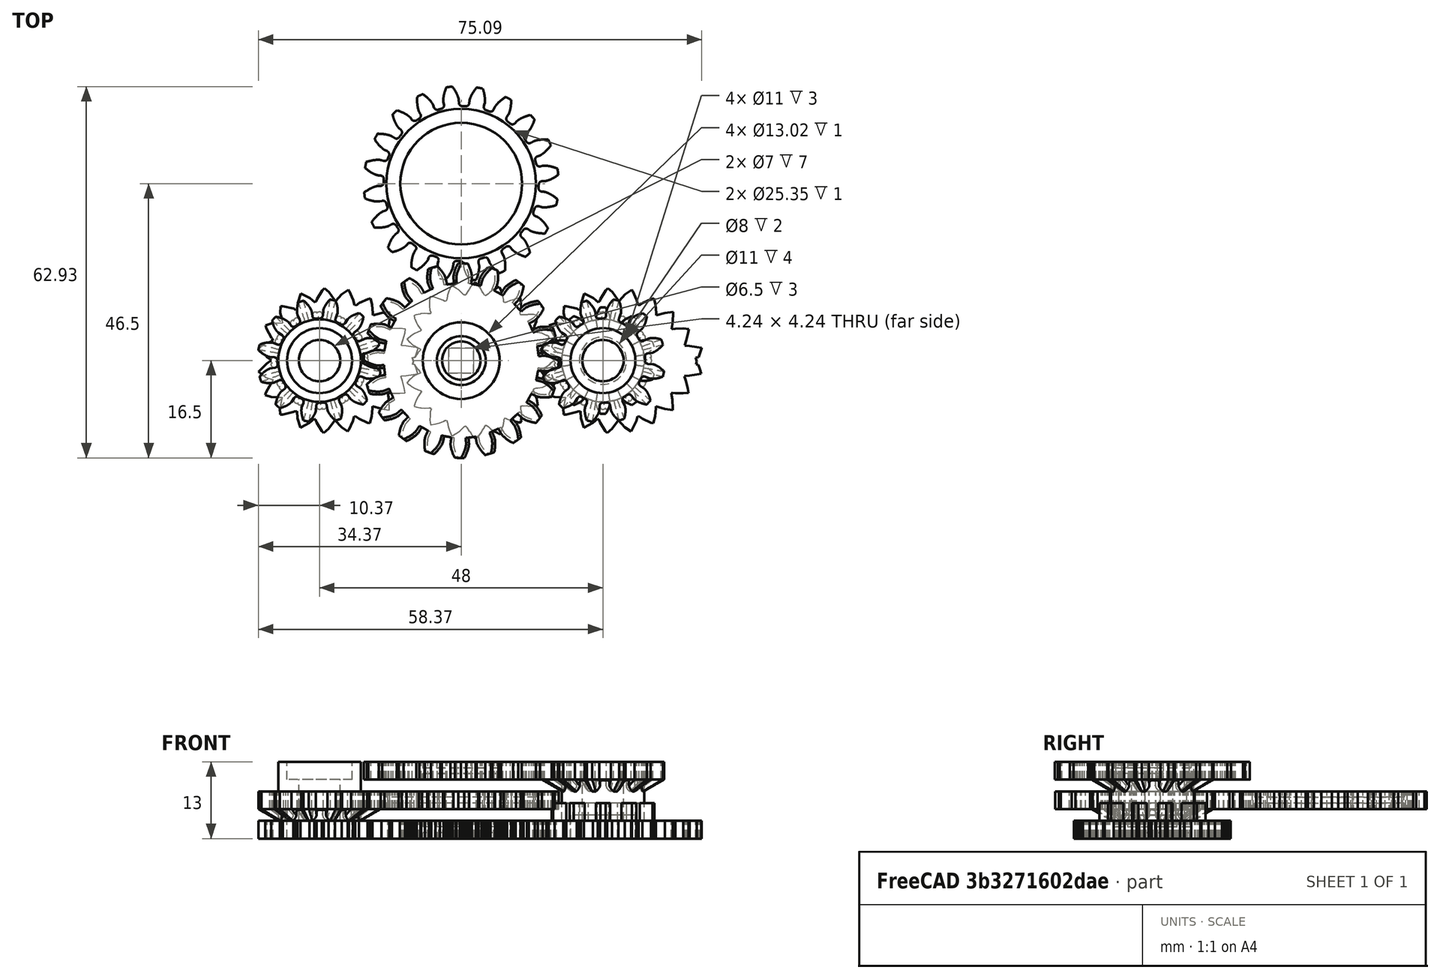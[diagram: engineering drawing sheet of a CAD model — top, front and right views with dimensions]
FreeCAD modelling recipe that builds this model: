
FCSTD DOCUMENT  (FreeCAD 0.16RUnknown)
Label: TriangleWaveGears
License: All rights reserved
LicenseURL: http://en.wikipedia.org/wiki/All_rights_reserved
objects: Sketcher::SketchObject×13, Part::Part2DObjectPython×11, Part::Cut×10, Part::Cylinder×9, PartDesign::Pad×8, Part::MultiFuse×7, PartDesign::Revolution×6, Part::FeaturePython×3, Mesh::Feature×2, Part::Loft×2
note: 83 computed .brp shape members not serialized (recipe doc carries the construction recipe); baked Part::Feature solids carry a one-line shape summary decoded from their .brp

FEATURE [Part::Part2DObjectPython] DWire  # Draft 2D object (typed FeaturePython)
  ChamferSize = 0
  Closed = true
  End = (40.7092,2.14552,0)
  FilletRadius = 0
  Length = 116.74
  MakeFace = true
  Placement = pos=(24,0,0) rot=(0,0,1;0rad)
  Points = (141) [(16.719,2.12868,0),(16.7092,2.14552,0),(15.8889,2.29087,0),(14.6751,2.46439,0),(13.876,2.52602,0),(13.8894,2.57671,0),(13.8323,2.58486,0),+134 more]
  Start = (40.719,2.12868,0)
  Subdivisions = 0
FEATURE [PartDesign::Pad] Pad
  Length = 3
  Length2 = 100
  Placement = pos=(24,0,0) rot=(0,0,1;0rad)
  Sketch = -> DWire
  Type = 0
FEATURE [Part::Part2DObjectPython] DWire001  # Draft 2D object (typed FeaturePython)
  ChamferSize = 0
  Closed = true
  End = (12.9776,-7.52391,0)
  FilletRadius = 0
  Length = 115.99
  MakeFace = true
  Points = (347) [(12.9407,-7.5751,0),(12.9776,-7.52391,0),(12.7586,-6.44106,0),(12.4722,-5.82977,0),(12.4305,-5.55586,0),(12.1811,-4.95491,0),(12.3268,-4.87553,0),+340 more]
  Start = (12.9407,-7.5751,0)
  Subdivisions = 0
FEATURE [PartDesign::Pad] Pad001
  Length = 3
  Length2 = 100
  Sketch = -> DWire001
  Type = 0
FEATURE [Sketcher::SketchObject] Sketch
  sketch-geometry (6):
    g0: LineSegment StartX=2.12132 StartY=2.12132 StartZ=0 EndX=-2.12132 EndY=2.12132 EndZ=0
    g1: LineSegment StartX=-2.12132 StartY=2.12132 StartZ=0 EndX=-2.12132 EndY=-2.12132 EndZ=0
    g2: LineSegment StartX=-2.12132 StartY=-2.12132 StartZ=0 EndX=2.12132 EndY=-2.12132 EndZ=0
    g3: LineSegment StartX=2.12132 StartY=-2.12132 StartZ=0 EndX=2.12132 EndY=2.12132 EndZ=0
    g4: Circle [constr] CenterX=0 CenterY=0 CenterZ=0 NormalX=0 NormalY=0 NormalZ=1 Radius=3
    g5: LineSegment [constr] StartX=0 StartY=0 StartZ=0 EndX=2.12132 EndY=2.12132 EndZ=0
  constraints (16):
    c: Coincident(g0,g1)
    c: Coincident(g1,g2)
    c: Coincident(g2,g3)
    c: Coincident(g3,g0)
    c: Equal(g0,g1)
    c: Equal(g0,g2)
    c: Equal(g0,g3)
    c: PointOnObject(g0,g4)
    c: PointOnObject(g1,g4)
    c: PointOnObject(g2,g4)
    c: PointOnObject(g3,g4)
    c: Coincident(g4,g-1)
    c: Radius(g4) = 3
    c: Coincident(g5,g-1)
    c: Coincident(g5,g0)
    c: Angle(g-1,g5) = 0.785398
FEATURE [PartDesign::Pad] Pad002
  Length = 10
  Length2 = 100
  Sketch = -> Sketch
  Type = 0
FEATURE [Part::Cut] Cut
  Base = -> Pad001
  Tool = -> Pad002
FEATURE [Sketcher::SketchObject] Sketch001
  Placement = pos=(24,0,0) rot=(0,0,1;0rad)
  sketch-geometry (1):
    g0: Circle CenterX=0 CenterY=0 CenterZ=0 NormalX=0 NormalY=0 NormalZ=1 Radius=5.5
  constraints (2):
    c: Coincident(g0,g-1)
    c: Radius(g0) = 5.5
FEATURE [PartDesign::Pad] Pad003
  Length = 4
  Length2 = 100
  Placement = pos=(24,0,0) rot=(0,0,1;0rad)
  Sketch = -> Sketch001
  Type = 0
FEATURE [Sketcher::SketchObject] Sketch002
  Placement = pos=(24,0,0) rot=(0,0,1;0rad)
  sketch-geometry (1):
    g0: Circle CenterX=0 CenterY=0 CenterZ=0 NormalX=0 NormalY=0 NormalZ=1 Radius=4
  constraints (2):
    c: Coincident(g0,g-1)
    c: Radius(g0) = 4
FEATURE [PartDesign::Pad] Pad004
  Length = 10
  Length2 = 100
  Placement = pos=(24,0,0) rot=(0,0,1;0rad)
  Sketch = -> Sketch002
  Type = 0
FEATURE [Part::FeaturePython] InvoluteGear  # WARN: FeaturePython — macro-defined, semantics opaque (R4)
  Placement = pos=(24,0,3) rot=(0,0,1;0.314159rad)
  backlash = 0
  beta = 0
  clearance = 0.25
  height = 3
  module = 1.5
  numpoints = 6
  pressure_angle = 20
  shift = 0
  simple = false
  teeth = 10
  undercut = false
FEATURE [Part::FeaturePython] InvoluteGear001  # WARN: FeaturePython — macro-defined, semantics opaque (R4)
  Placement = pos=(0,0,9) rot=(0,0,1;0.087266rad)
  backlash = 0
  beta = 0
  clearance = 0.25
  height = 3
  module = 1.5
  numpoints = 6
  pressure_angle = 20
  shift = 0
  simple = false
  teeth = 20
  undercut = false
FEATURE [Mesh::Feature] PD_inner_gear
  Placement = pos=(0,-33,7) rot=(0,0,1;0rad)
FEATURE [Part::FeaturePython] InvoluteGear002  # WARN: FeaturePython — macro-defined, semantics opaque (R4)
  Placement = pos=(0,0,5) rot=(0,0,1;0rad)
  backlash = 0
  beta = 0
  clearance = 0.25
  height = 3
  module = 1.5
  numpoints = 6
  pressure_angle = 20
  shift = 0
  simple = false
  teeth = 20
  undercut = false
FEATURE [Mesh::Feature] PD_inner_gear001
  Placement = pos=(0,-33,11) rot=(0,0,1;0rad)
FEATURE [Part::MultiFuse] Fusion
  Shapes = -> [Pad004,Pad003]
FEATURE [Part::MultiFuse] Fusion001
  Shapes = -> [InvoluteGear,Pad]
FEATURE [Part::Cut] Cut001
  Base = -> Fusion001
  Tool = -> Fusion
FEATURE [Sketcher::SketchObject] Sketch003
  Placement = pos=(0,0,8) rot=(1,0,0;1.5708rad)
  sketch-geometry (16):
    g0: Circle [constr] CenterX=0 CenterY=0 CenterZ=0 NormalX=0 NormalY=0 NormalZ=1 Radius=5.3242
    g1: Circle [constr] CenterX=5.3242 CenterY=0 CenterZ=0 NormalX=0 NormalY=0 NormalZ=1 Radius=1.5
    g2: Circle [constr] CenterX=4.479 CenterY=-2.87848 CenterZ=0 NormalX=0 NormalY=0 NormalZ=1 Radius=1.5
    g3: LineSegment [constr] StartX=0 StartY=0 StartZ=0 EndX=4.479 EndY=-2.87848 EndZ=0
    g4: LineSegment StartX=4.13993 StartY=1 StartZ=0 EndX=6.50847 EndY=1 EndZ=0
    g5: LineSegment StartX=6.50847 StartY=1 StartZ=0 EndX=6.50847 EndY=2 EndZ=0
    g6: LineSegment StartX=6.50847 StartY=2 StartZ=0 EndX=4.13993 EndY=2 EndZ=0
    g7: LineSegment StartX=4.13993 StartY=2 StartZ=0 EndX=4.13993 EndY=1 EndZ=0
    g8: LineSegment [constr] StartX=4.13993 StartY=-1 StartZ=0 EndX=6.50847 EndY=-1 EndZ=0
    g9: LineSegment [constr] StartX=6.50847 StartY=-1 StartZ=0 EndX=6.50847 EndY=-2 EndZ=0
    g10: LineSegment [constr] StartX=6.50847 StartY=-2 StartZ=0 EndX=4.13993 EndY=-2 EndZ=0
    g11: LineSegment [constr] StartX=4.13993 StartY=-2 StartZ=0 EndX=4.13993 EndY=-1 EndZ=0
    g12: LineSegment [constr] StartX=5.3242 StartY=0 StartZ=0 EndX=5.3242 EndY=2 EndZ=0
    g13: Circle [constr] CenterX=5.3242 CenterY=0 CenterZ=0 NormalX=0 NormalY=0 NormalZ=1 Radius=1.55
    g14: LineSegment [constr] StartX=5.3242 StartY=0 StartZ=0 EndX=6.769 EndY=-0.403161 EndZ=0
    g15: LineSegment [constr] StartX=6.769 StartY=-0.403161 StartZ=0 EndX=6.81716 EndY=-0.416599 EndZ=0
  constraints (42):
    c: Coincident(g0,g-1)
    c: PointOnObject(g1,g0)
    c: PointOnObject(g2,g0)
    c: Tangent(g1,g2)
    c: Equal(g1,g2)
    c: Coincident(g3,g-1)
    c: Coincident(g3,g2)
    c: Angle(g3,g-1) = 0.571199
    c: Radius(g1) = 1.5
    c: PointOnObject(g1,g-1)
    c: Horizontal(g4)
    c: Coincident(g4,g5)
    c: Vertical(g5)
    c: Coincident(g5,g6)
    c: Coincident(g6,g7)
    c: Coincident(g7,g4)
    c: Vertical(g7)
    c: Horizontal(g6)
    c: Coincident(g8,g9)
    c: Coincident(g9,g10)
    c: Coincident(g10,g11)
    c: Coincident(g11,g8)
    c: Horizontal(g8)
    c: Horizontal(g10)
    c: Vertical(g9)
    c: Vertical(g11)
    c: Symmetric(g8,g4,g-1)
    c: DistanceY(g8,g4) = 2
    c: Coincident(g12,g1)
    c: PointOnObject(g12,g6)
    c: Symmetric(g6,g5,g12)
    c: Equal(g4,g8)
    c: Equal(g5,g9)
    c: DistanceY(g5,g5) = 1
    c: Coincident(g13,g1)
    c: Coincident(g14,g1)
    c: Coincident(g14,g15)
    c: PointOnObject(g15,g13)
    c: PointOnObject(g14,g1)
    c: Parallel(g15,g14)
    c: Distance(g15) = 0.05
    c: PointOnObject(g4,g13)
FEATURE [PartDesign::Revolution] Revolution
  Angle = 360
  Axis = (0,0,1)
  Base = (0,0,8)
  Placement = pos=(0,0,8) rot=(1,0,0;1.5708rad)
  ReferenceAxis = -> Sketch003 [V_Axis]
  Reversed = true
  Sketch = -> Sketch003
FEATURE [Part::Cut] Cut002
  Base = -> InvoluteGear001
  Tool = -> Revolution
FEATURE [Sketcher::SketchObject] Sketch004
  Placement = pos=(0,0,13) rot=(1,0,0;1.5708rad)
  sketch-geometry (16):
    g0: Circle [constr] CenterX=0 CenterY=0 CenterZ=0 NormalX=0 NormalY=0 NormalZ=1 Radius=5.3242
    g1: Circle [constr] CenterX=5.3242 CenterY=0 CenterZ=0 NormalX=0 NormalY=0 NormalZ=1 Radius=1.5
    g2: Circle [constr] CenterX=4.479 CenterY=-2.87848 CenterZ=0 NormalX=0 NormalY=0 NormalZ=1 Radius=1.5
    g3: LineSegment [constr] StartX=0 StartY=0 StartZ=0 EndX=4.479 EndY=-2.87848 EndZ=0
    g4: LineSegment [constr] StartX=4.13993 StartY=1 StartZ=0 EndX=6.50847 EndY=1 EndZ=0
    g5: LineSegment [constr] StartX=6.50847 StartY=1 StartZ=0 EndX=6.50847 EndY=2 EndZ=0
    g6: LineSegment [constr] StartX=6.50847 StartY=2 StartZ=0 EndX=4.13993 EndY=2 EndZ=0
    g7: LineSegment [constr] StartX=4.13993 StartY=2 StartZ=0 EndX=4.13993 EndY=1 EndZ=0
    g8: LineSegment StartX=4.13993 StartY=-1 StartZ=0 EndX=6.50847 EndY=-1 EndZ=0
    g9: LineSegment StartX=6.50847 StartY=-1 StartZ=0 EndX=6.50847 EndY=-2 EndZ=0
    g10: LineSegment StartX=6.50847 StartY=-2 StartZ=0 EndX=4.13993 EndY=-2 EndZ=0
    g11: LineSegment StartX=4.13993 StartY=-2 StartZ=0 EndX=4.13993 EndY=-1 EndZ=0
    g12: LineSegment [constr] StartX=5.3242 StartY=0 StartZ=0 EndX=5.3242 EndY=2 EndZ=0
    g13: Circle [constr] CenterX=5.3242 CenterY=0 CenterZ=0 NormalX=0 NormalY=0 NormalZ=1 Radius=1.55
    g14: LineSegment [constr] StartX=5.3242 StartY=0 StartZ=0 EndX=6.769 EndY=-0.403179 EndZ=0
    g15: LineSegment [constr] StartX=6.769 StartY=-0.403179 StartZ=0 EndX=6.81716 EndY=-0.416618 EndZ=0
  constraints (42):
    c: Coincident(g0,g-1)
    c: PointOnObject(g1,g0)
    c: PointOnObject(g2,g0)
    c: Tangent(g1,g2)
    c: Equal(g1,g2)
    c: Coincident(g3,g-1)
    c: Coincident(g3,g2)
    c: Angle(g3,g-1) = 0.571199
    c: Radius(g1) = 1.5
    c: PointOnObject(g1,g-1)
    c: Horizontal(g4)
    c: Coincident(g4,g5)
    c: Vertical(g5)
    c: Coincident(g5,g6)
    c: Coincident(g6,g7)
    c: Coincident(g7,g4)
    c: Vertical(g7)
    c: Horizontal(g6)
    c: Coincident(g8,g9)
    c: Coincident(g9,g10)
    c: Coincident(g10,g11)
    c: Coincident(g11,g8)
    c: Horizontal(g8)
    c: Horizontal(g10)
    c: Vertical(g9)
    c: Vertical(g11)
    c: Symmetric(g8,g4,g-1)
    c: DistanceY(g8,g4) = 2
    c: Coincident(g12,g1)
    c: PointOnObject(g12,g6)
    c: Symmetric(g6,g5,g12)
    c: Equal(g4,g8)
    c: Equal(g5,g9)
    c: DistanceY(g5,g5) = 1
    c: Coincident(g13,g1)
    c: Coincident(g14,g1)
    c: Coincident(g14,g15)
    c: PointOnObject(g15,g13)
    c: PointOnObject(g14,g1)
    c: Parallel(g15,g14)
    c: Distance(g15) = 0.05
    c: PointOnObject(g4,g13)
FEATURE [PartDesign::Revolution] Revolution001
  Angle = 360
  Axis = (0,0,1)
  Base = (0,0,13)
  Placement = pos=(0,0,13) rot=(1,0,0;1.5708rad)
  ReferenceAxis = -> Sketch004 [V_Axis]
  Reversed = true
  Sketch = -> Sketch004
FEATURE [Part::Cut] Cut003
  Base = -> Cut002
  Placement = pos=(0,0,1) rot=(0,0,1;0.191986rad)
  Tool = -> Revolution001
FEATURE [Sketcher::SketchObject] Sketch005
  sketch-geometry (1):
    g0: Circle CenterX=0 CenterY=0 CenterZ=0 NormalX=0 NormalY=0 NormalZ=1 Radius=4.5
  constraints (2):
    c: Coincident(g0,g-1)
    c: Radius(g0) = 4.5
FEATURE [Sketcher::SketchObject] Sketch007
  Placement = pos=(0,0,4) rot=(1,0,0;1.5708rad)
  sketch-geometry (16):
    g0: Circle [constr] CenterX=0 CenterY=0 CenterZ=0 NormalX=0 NormalY=0 NormalZ=1 Radius=5.3242
    g1: Circle [constr] CenterX=5.3242 CenterY=0 CenterZ=0 NormalX=0 NormalY=0 NormalZ=1 Radius=1.5
    g2: Circle [constr] CenterX=4.479 CenterY=-2.87848 CenterZ=0 NormalX=0 NormalY=0 NormalZ=1 Radius=1.5
    g3: LineSegment [constr] StartX=0 StartY=0 StartZ=0 EndX=4.479 EndY=-2.87848 EndZ=0
    g4: LineSegment [constr] StartX=4.13993 StartY=1 StartZ=0 EndX=6.50847 EndY=1 EndZ=0
    g5: LineSegment [constr] StartX=6.50847 StartY=1 StartZ=0 EndX=6.50847 EndY=2 EndZ=0
    g6: LineSegment [constr] StartX=6.50847 StartY=2 StartZ=0 EndX=4.13993 EndY=2 EndZ=0
    g7: LineSegment [constr] StartX=4.13993 StartY=2 StartZ=0 EndX=4.13993 EndY=1 EndZ=0
    g8: LineSegment StartX=4.13993 StartY=-1 StartZ=0 EndX=6.50847 EndY=-1 EndZ=0
    g9: LineSegment StartX=6.50847 StartY=-1 StartZ=0 EndX=6.50847 EndY=-2 EndZ=0
    g10: LineSegment StartX=6.50847 StartY=-2 StartZ=0 EndX=4.13993 EndY=-2 EndZ=0
    g11: LineSegment StartX=4.13993 StartY=-2 StartZ=0 EndX=4.13993 EndY=-1 EndZ=0
    g12: LineSegment [constr] StartX=5.3242 StartY=0 StartZ=0 EndX=5.3242 EndY=2 EndZ=0
    g13: Circle [constr] CenterX=5.3242 CenterY=0 CenterZ=0 NormalX=0 NormalY=0 NormalZ=1 Radius=1.55
    g14: LineSegment [constr] StartX=5.3242 StartY=0 StartZ=0 EndX=6.769 EndY=-0.403179 EndZ=0
    g15: LineSegment [constr] StartX=6.769 StartY=-0.403179 StartZ=0 EndX=6.81716 EndY=-0.416618 EndZ=0
  constraints (42):
    c: Coincident(g0,g-1)
    c: PointOnObject(g1,g0)
    c: PointOnObject(g2,g0)
    c: Tangent(g1,g2)
    c: Equal(g1,g2)
    c: Coincident(g3,g-1)
    c: Coincident(g3,g2)
    c: Angle(g3,g-1) = 0.571199
    c: Radius(g1) = 1.5
    c: PointOnObject(g1,g-1)
    c: Horizontal(g4)
    c: Coincident(g4,g5)
    c: Vertical(g5)
    c: Coincident(g5,g6)
    c: Coincident(g6,g7)
    c: Coincident(g7,g4)
    c: Vertical(g7)
    c: Horizontal(g6)
    c: Coincident(g8,g9)
    c: Coincident(g9,g10)
    c: Coincident(g10,g11)
    c: Coincident(g11,g8)
    c: Horizontal(g8)
    c: Horizontal(g10)
    c: Vertical(g9)
    c: Vertical(g11)
    c: Symmetric(g8,g4,g-1)
    c: DistanceY(g8,g4) = 2
    c: Coincident(g12,g1)
    c: PointOnObject(g12,g6)
    c: Symmetric(g6,g5,g12)
    c: Equal(g4,g8)
    c: Equal(g5,g9)
    c: DistanceY(g5,g5) = 1
    c: Coincident(g13,g1)
    c: Coincident(g14,g1)
    c: Coincident(g14,g15)
    c: PointOnObject(g15,g13)
    c: PointOnObject(g14,g1)
    c: Parallel(g15,g14)
    c: Distance(g15) = 0.05
    c: PointOnObject(g4,g13)
FEATURE [Sketcher::SketchObject] Sketch008
  Placement = pos=(0,0,-1) rot=(1,0,0;1.5708rad)
  sketch-geometry (16):
    g0: Circle [constr] CenterX=0 CenterY=0 CenterZ=0 NormalX=0 NormalY=0 NormalZ=1 Radius=5.3242
    g1: Circle [constr] CenterX=5.3242 CenterY=0 CenterZ=0 NormalX=0 NormalY=0 NormalZ=1 Radius=1.5
    g2: Circle [constr] CenterX=4.479 CenterY=-2.87848 CenterZ=0 NormalX=0 NormalY=0 NormalZ=1 Radius=1.5
    g3: LineSegment [constr] StartX=0 StartY=0 StartZ=0 EndX=4.479 EndY=-2.87848 EndZ=0
    g4: LineSegment StartX=4.13993 StartY=1 StartZ=0 EndX=6.50847 EndY=1 EndZ=0
    g5: LineSegment StartX=6.50847 StartY=1 StartZ=0 EndX=6.50847 EndY=2 EndZ=0
    g6: LineSegment StartX=6.50847 StartY=2 StartZ=0 EndX=4.13993 EndY=2 EndZ=0
    g7: LineSegment StartX=4.13993 StartY=2 StartZ=0 EndX=4.13993 EndY=1 EndZ=0
    g8: LineSegment [constr] StartX=4.13993 StartY=-1 StartZ=0 EndX=6.50847 EndY=-1 EndZ=0
    g9: LineSegment [constr] StartX=6.50847 StartY=-1 StartZ=0 EndX=6.50847 EndY=-2 EndZ=0
    g10: LineSegment [constr] StartX=6.50847 StartY=-2 StartZ=0 EndX=4.13993 EndY=-2 EndZ=0
    g11: LineSegment [constr] StartX=4.13993 StartY=-2 StartZ=0 EndX=4.13993 EndY=-1 EndZ=0
    g12: LineSegment [constr] StartX=5.3242 StartY=0 StartZ=0 EndX=5.3242 EndY=2 EndZ=0
    g13: Circle [constr] CenterX=5.3242 CenterY=0 CenterZ=0 NormalX=0 NormalY=0 NormalZ=1 Radius=1.55
    g14: LineSegment [constr] StartX=5.3242 StartY=0 StartZ=0 EndX=6.769 EndY=-0.403161 EndZ=0
    g15: LineSegment [constr] StartX=6.769 StartY=-0.403161 StartZ=0 EndX=6.81716 EndY=-0.416599 EndZ=0
  constraints (42):
    c: Coincident(g0,g-1)
    c: PointOnObject(g1,g0)
    c: PointOnObject(g2,g0)
    c: Tangent(g1,g2)
    c: Equal(g1,g2)
    c: Coincident(g3,g-1)
    c: Coincident(g3,g2)
    c: Angle(g3,g-1) = 0.571199
    c: Radius(g1) = 1.5
    c: PointOnObject(g1,g-1)
    c: Horizontal(g4)
    c: Coincident(g4,g5)
    c: Vertical(g5)
    c: Coincident(g5,g6)
    c: Coincident(g6,g7)
    c: Coincident(g7,g4)
    c: Vertical(g7)
    c: Horizontal(g6)
    c: Coincident(g8,g9)
    c: Coincident(g9,g10)
    c: Coincident(g10,g11)
    c: Coincident(g11,g8)
    c: Horizontal(g8)
    c: Horizontal(g10)
    c: Vertical(g9)
    c: Vertical(g11)
    c: Symmetric(g8,g4,g-1)
    c: DistanceY(g8,g4) = 2
    c: Coincident(g12,g1)
    c: PointOnObject(g12,g6)
    c: Symmetric(g6,g5,g12)
    c: Equal(g4,g8)
    c: Equal(g5,g9)
    c: DistanceY(g5,g5) = 1
    c: Coincident(g13,g1)
    c: Coincident(g14,g1)
    c: Coincident(g14,g15)
    c: PointOnObject(g15,g13)
    c: PointOnObject(g14,g1)
    c: Parallel(g15,g14)
    c: Distance(g15) = 0.05
    c: PointOnObject(g4,g13)
FEATURE [PartDesign::Revolution] Revolution002
  Angle = 360
  Axis = (0,0,1)
  Base = (0,0,4)
  Placement = pos=(0,0,4) rot=(1,0,0;1.5708rad)
  ReferenceAxis = -> Sketch007 [V_Axis]
  Reversed = true
  Sketch = -> Sketch007
FEATURE [PartDesign::Revolution] Revolution003
  Angle = 360
  Axis = (0,0,1)
  Base = (0,0,-1)
  Placement = pos=(0,0,-1) rot=(1,0,0;1.5708rad)
  ReferenceAxis = -> Sketch008 [V_Axis]
  Reversed = true
  Sketch = -> Sketch008
FEATURE [Part::MultiFuse] Fusion002
  Shapes = -> [Revolution003,Revolution002]
FEATURE [Part::Cut] Cut004
  Base = -> Cut
  Tool = -> Fusion002
FEATURE [Part::Part2DObjectPython] DWire002  label="g1base"  # Draft 2D object (typed FeaturePython)
  ChamferSize = 0
  Closed = true
  End = (40.7092,2.14552,0)
  FilletRadius = 0
  Length = 116.74
  MakeFace = true
  Placement = pos=(24,0,0) rot=(0,0,1;0rad)
  Points = (141) [(16.719,2.12868,0),(16.7092,2.14552,0),(15.8889,2.29087,0),(14.6751,2.46439,0),(13.876,2.52602,0),(13.8894,2.57671,0),(13.8323,2.58486,0),+134 more]
  Start = (40.719,2.12868,0)
  Subdivisions = 0
FEATURE [Part::Part2DObjectPython] InvoluteGear003  label="g1base2"  # Draft 2D object (typed FeaturePython)
  ExternalGear = true
  HighPrecision = true
  Modules = 1
  NumberOfTeeth = 12
  Placement = pos=(24,0,8) rot=(0,0,1;0.305433rad)
  PressureAngle = 20
FEATURE [Part::Part2DObjectPython] InvoluteGear004  label="g1top2"  # Draft 2D object (typed FeaturePython)
  ExternalGear = true
  HighPrecision = true
  Modules = 1.5
  NumberOfTeeth = 12
  Placement = pos=(24,0,13) rot=(0,0,1;0.305433rad)
  PressureAngle = 20
FEATURE [Part::Part2DObjectPython] DWire003  label="g2base"  # Draft 2D object (typed FeaturePython)
  ChamferSize = 0
  Closed = true
  End = (-7.29077,2.14552,0)
  FilletRadius = 0
  Length = 116.74
  MakeFace = true
  Placement = pos=(-24,0,0) rot=(0,0,1;0rad)
  Points = (141) [(16.719,2.12868,0),(16.7092,2.14552,0),(15.8889,2.29087,0),(14.6751,2.46439,0),(13.876,2.52602,0),(13.8894,2.57671,0),(13.8323,2.58486,0),+134 more]
  Start = (-7.28098,2.12868,0)
  Subdivisions = 0
FEATURE [Part::Part2DObjectPython] InvoluteGear005  label="g1base2mid"  # Draft 2D object (typed FeaturePython)
  ExternalGear = true
  HighPrecision = true
  Modules = 1.5
  NumberOfTeeth = 12
  Placement = pos=(24,0,10) rot=(0,0,1;0.305433rad)
  PressureAngle = 20
FEATURE [PartDesign::Pad] Pad005  label="bottomgear"
  Length = 3
  Length2 = 100
  Placement = pos=(24,0,0) rot=(0,0,1;0rad)
  Sketch = -> DWire002
  Type = 0
FEATURE [Sketcher::SketchObject] Sketch009
FEATURE [Part::Cylinder] Cylinder  label="spacer"
  Angle = 360
  Height = 10
  Placement = pos=(24,0,0) rot=(0,0,1;0rad)
  Radius = 7
FEATURE [Part::Loft] Loft  label="topgear"
  Closed = false
  Ruled = true
  Sections = -> [InvoluteGear003,InvoluteGear005,InvoluteGear004]
  Solid = true
FEATURE [PartDesign::Pad] Pad006  label="bottogear"
  Length = 3
  Length2 = 100
  Placement = pos=(-24,0,0) rot=(0,0,1;0rad)
  Sketch = -> DWire003
  Type = 0
FEATURE [Part::Part2DObjectPython] InvoluteGear006  label="g3top"  # Draft 2D object (typed FeaturePython)
  ExternalGear = true
  HighPrecision = true
  Modules = 1.5
  NumberOfTeeth = 12
  Placement = pos=(-24,0,8) rot=(0,0,1;0.305433rad)
  PressureAngle = 20
FEATURE [Part::Part2DObjectPython] InvoluteGear007  label="g3mid"  # Draft 2D object (typed FeaturePython)
  ExternalGear = true
  HighPrecision = true
  Modules = 1.5
  NumberOfTeeth = 12
  Placement = pos=(-24,0,5) rot=(0,0,1;0.305433rad)
  PressureAngle = 20
FEATURE [Part::Part2DObjectPython] InvoluteGear008  label="g3small"  # Draft 2D object (typed FeaturePython)
  ExternalGear = true
  HighPrecision = true
  Modules = 1
  NumberOfTeeth = 12
  Placement = pos=(-24,0,3) rot=(0,0,1;0.305433rad)
  PressureAngle = 20
FEATURE [Part::Loft] Loft001  label="topgear"
  Closed = false
  Ruled = true
  Sections = -> [InvoluteGear008,InvoluteGear007,InvoluteGear006]
  Solid = true
FEATURE [Part::Cylinder] Cylinder001  label="axleCutout"
  Angle = 360
  Height = 20
  Placement = pos=(24,0,0) rot=(0,0,1;0rad)
  Radius = 3.5
FEATURE [Part::Cylinder] Cylinder002  label="axleCutout"
  Angle = 360
  Height = 20
  Placement = pos=(-24,0,0) rot=(0,0,1;0rad)
  Radius = 3.5
FEATURE [Part::Cylinder] Cylinder003  label="topSpacer"
  Angle = 360
  Height = 13
  Placement = pos=(-24,0,0) rot=(0,0,1;0rad)
  Radius = 7
FEATURE [Part::Cylinder] Cylinder004  label="bearingCutoutTop"
  Angle = 360
  Height = 3
  Placement = pos=(-24,0,10) rot=(0,0,1;0rad)
  Radius = 5.5
FEATURE [Part::Cylinder] Cylinder005  label="bearingCutoutBot"
  Angle = 360
  Height = 3
  Placement = pos=(-24,0,0) rot=(0,0,1;0rad)
  Radius = 5.5
FEATURE [Part::MultiFuse] Fusion003  label="base"
  Shapes = -> [Pad006,Loft001,Cylinder003]
FEATURE [Part::MultiFuse] Fusion004  label="cutouts"
  Shapes = -> [Cylinder005,Cylinder004,Cylinder002]
FEATURE [Part::Cut] Cut005
  Base = -> Fusion003
  Tool = -> Fusion004
FEATURE [Part::MultiFuse] Fusion005  label="base"
  Shapes = -> [Pad005,Cylinder,Loft]
FEATURE [Part::Cylinder] Cylinder006  label="bearingCutoutBot"
  Angle = 360
  Height = 3
  Placement = pos=(24,0,0) rot=(0,0,1;0rad)
  Radius = 5.5
FEATURE [Part::Cylinder] Cylinder007  label="bearingCutoutTop"
  Angle = 360
  Height = 3
  Placement = pos=(24,0,10) rot=(0,0,1;0rad)
  Radius = 5.5
FEATURE [Part::MultiFuse] Fusion006  label="cutouts"
  Shapes = -> [Cylinder007,Cylinder006,Cylinder001]
FEATURE [Part::Cut] Cut006
  Base = -> Fusion005
  Tool = -> Fusion006
FEATURE [Part::Cylinder] Cylinder008  label="Cylinder"
  Angle = 360
  Height = 60
  Radius = 3.25
FEATURE [Part::Cut] Cut007
  Base = -> Cut003
  Tool = -> Cylinder008
FEATURE [Part::Part2DObjectPython] InvoluteGear009  # Draft 2D object (typed FeaturePython)
  ExternalGear = true
  HighPrecision = true
  Modules = 1.5
  NumberOfTeeth = 20
  Placement = pos=(0,30,5) rot=(0,0,-1;0.191986rad)
  PressureAngle = 20
FEATURE [PartDesign::Pad] Pad007
  Length = 3
  Length2 = 100
  Placement = pos=(0,30,5) rot=(0,0,-1;0.191986rad)
  Sketch = -> InvoluteGear009
  Type = 0
FEATURE [Sketcher::SketchObject] Sketch010
  Placement = pos=(0,30,4) rot=(1,0,0;1.5708rad)
  sketch-geometry (16):
    g0: Circle [constr] CenterX=0 CenterY=0 CenterZ=0 NormalX=0 NormalY=0 NormalZ=1 Radius=11.4919
    g1: Circle [constr] CenterX=11.4919 CenterY=0 CenterZ=0 NormalX=0 NormalY=0 NormalZ=1 Radius=1.5
    g2: Circle [constr] CenterX=11.1004 CenterY=-2.97433 CenterZ=0 NormalX=0 NormalY=0 NormalZ=1 Radius=1.5
    g3: LineSegment [constr] StartX=0 StartY=0 StartZ=0 EndX=11.1004 EndY=-2.97433 EndZ=0
    g4: LineSegment StartX=10.3077 StartY=1 StartZ=0 EndX=12.6762 EndY=1 EndZ=0
    g5: LineSegment StartX=12.6762 StartY=1 StartZ=0 EndX=12.6762 EndY=2 EndZ=0
    g6: LineSegment StartX=12.6762 StartY=2 StartZ=0 EndX=10.3077 EndY=2 EndZ=0
    g7: LineSegment StartX=10.3077 StartY=2 StartZ=0 EndX=10.3077 EndY=1 EndZ=0
    g8: LineSegment [constr] StartX=10.3077 StartY=-1 StartZ=0 EndX=12.6762 EndY=-1 EndZ=0
    g9: LineSegment [constr] StartX=12.6762 StartY=-1 StartZ=0 EndX=12.6762 EndY=-2 EndZ=0
    g10: LineSegment [constr] StartX=12.6762 StartY=-2 StartZ=0 EndX=10.3077 EndY=-2 EndZ=0
    g11: LineSegment [constr] StartX=10.3077 StartY=-2 StartZ=0 EndX=10.3077 EndY=-1 EndZ=0
    g12: LineSegment [constr] StartX=11.4919 StartY=0 StartZ=0 EndX=11.4919 EndY=2 EndZ=0
    g13: Circle [constr] CenterX=11.4919 CenterY=0 CenterZ=0 NormalX=0 NormalY=0 NormalZ=1 Radius=1.55
    g14: LineSegment [constr] StartX=11.4919 StartY=0 StartZ=0 EndX=12.9367 EndY=-0.403202 EndZ=0
    g15: LineSegment [constr] StartX=12.9367 StartY=-0.403202 StartZ=0 EndX=12.9849 EndY=-0.416642 EndZ=0
  constraints (42):
    c: Coincident(g0,g-1)
    c: PointOnObject(g1,g0)
    c: PointOnObject(g2,g0)
    c: Tangent(g1,g2)
    c: Equal(g1,g2)
    c: Coincident(g3,g-1)
    c: Coincident(g3,g2)
    c: Angle(g3,g-1) = 0.261799
    c: Radius(g1) = 1.5
    c: PointOnObject(g1,g-1)
    c: Horizontal(g4)
    c: Coincident(g4,g5)
    c: Vertical(g5)
    c: Coincident(g5,g6)
    c: Coincident(g6,g7)
    c: Coincident(g7,g4)
    c: Vertical(g7)
    c: Horizontal(g6)
    c: Coincident(g8,g9)
    c: Coincident(g9,g10)
    c: Coincident(g10,g11)
    c: Coincident(g11,g8)
    c: Horizontal(g8)
    c: Horizontal(g10)
    c: Vertical(g9)
    c: Vertical(g11)
    c: Symmetric(g8,g4,g-1)
    c: DistanceY(g8,g4) = 2
    c: Coincident(g12,g1)
    c: PointOnObject(g12,g6)
    c: Symmetric(g6,g5,g12)
    c: Equal(g4,g8)
    c: Equal(g5,g9)
    c: DistanceY(g5,g5) = 1
    c: Coincident(g13,g1)
    c: Coincident(g14,g1)
    c: Coincident(g14,g15)
    c: PointOnObject(g15,g13)
    c: PointOnObject(g14,g1)
    c: Parallel(g15,g14)
    c: Distance(g15) = 0.05
    c: PointOnObject(g4,g13)
FEATURE [PartDesign::Revolution] Revolution004
  Angle = 360
  Axis = (0,0,1)
  Base = (0,30,4)
  Placement = pos=(0,30,4) rot=(1,0,0;1.5708rad)
  ReferenceAxis = -> Sketch010 [V_Axis]
  Reversed = true
  Sketch = -> Sketch010
FEATURE [Part::Cut] Cut008
  Base = -> Pad007
  Tool = -> Revolution004
FEATURE [Sketcher::SketchObject] Sketch011
  Placement = pos=(0,30,9) rot=(1,0,0;1.5708rad)
  sketch-geometry (16):
    g0: Circle [constr] CenterX=0 CenterY=0 CenterZ=0 NormalX=0 NormalY=0 NormalZ=1 Radius=11.4919
    g1: Circle [constr] CenterX=11.4919 CenterY=0 CenterZ=0 NormalX=0 NormalY=0 NormalZ=1 Radius=1.5
    g2: Circle [constr] CenterX=11.1004 CenterY=-2.97433 CenterZ=0 NormalX=0 NormalY=0 NormalZ=1 Radius=1.5
    g3: LineSegment [constr] StartX=0 StartY=0 StartZ=0 EndX=11.1004 EndY=-2.97433 EndZ=0
    g4: LineSegment [constr] StartX=10.3077 StartY=1 StartZ=0 EndX=12.6762 EndY=1 EndZ=0
    g5: LineSegment [constr] StartX=12.6762 StartY=1 StartZ=0 EndX=12.6762 EndY=2 EndZ=0
    g6: LineSegment [constr] StartX=12.6762 StartY=2 StartZ=0 EndX=10.3077 EndY=2 EndZ=0
    g7: LineSegment [constr] StartX=10.3077 StartY=2 StartZ=0 EndX=10.3077 EndY=1 EndZ=0
    g8: LineSegment StartX=10.3077 StartY=-1 StartZ=0 EndX=12.6762 EndY=-1 EndZ=0
    g9: LineSegment StartX=12.6762 StartY=-1 StartZ=0 EndX=12.6762 EndY=-2 EndZ=0
    g10: LineSegment StartX=12.6762 StartY=-2 StartZ=0 EndX=10.3077 EndY=-2 EndZ=0
    g11: LineSegment StartX=10.3077 StartY=-2 StartZ=0 EndX=10.3077 EndY=-1 EndZ=0
    g12: LineSegment [constr] StartX=11.4919 StartY=0 StartZ=0 EndX=11.4919 EndY=2 EndZ=0
    g13: Circle [constr] CenterX=11.4919 CenterY=0 CenterZ=0 NormalX=0 NormalY=0 NormalZ=1 Radius=1.55
    g14: LineSegment [constr] StartX=11.4919 StartY=0 StartZ=0 EndX=12.9367 EndY=-0.403202 EndZ=0
    g15: LineSegment [constr] StartX=12.9367 StartY=-0.403202 StartZ=0 EndX=12.9849 EndY=-0.416642 EndZ=0
  constraints (42):
    c: Coincident(g0,g-1)
    c: PointOnObject(g1,g0)
    c: PointOnObject(g2,g0)
    c: Tangent(g1,g2)
    c: Equal(g1,g2)
    c: Coincident(g3,g-1)
    c: Coincident(g3,g2)
    c: Angle(g3,g-1) = 0.261799
    c: Radius(g1) = 1.5
    c: PointOnObject(g1,g-1)
    c: Horizontal(g4)
    c: Coincident(g4,g5)
    c: Vertical(g5)
    c: Coincident(g5,g6)
    c: Coincident(g6,g7)
    c: Coincident(g7,g4)
    c: Vertical(g7)
    c: Horizontal(g6)
    c: Coincident(g8,g9)
    c: Coincident(g9,g10)
    c: Coincident(g10,g11)
    c: Coincident(g11,g8)
    c: Horizontal(g8)
    c: Horizontal(g10)
    c: Vertical(g9)
    c: Vertical(g11)
    c: Symmetric(g8,g4,g-1)
    c: DistanceY(g8,g4) = 2
    c: Coincident(g12,g1)
    c: PointOnObject(g12,g6)
    c: Symmetric(g6,g5,g12)
    c: Equal(g4,g8)
    c: Equal(g5,g9)
    c: DistanceY(g5,g5) = 1
    c: Coincident(g13,g1)
    c: Coincident(g14,g1)
    c: Coincident(g14,g15)
    c: PointOnObject(g15,g13)
    c: PointOnObject(g14,g1)
    c: Parallel(g15,g14)
    c: Distance(g15) = 0.05
    c: PointOnObject(g4,g13)
FEATURE [PartDesign::Revolution] Revolution005
  Angle = 360
  Axis = (0,0,1)
  Base = (0,30,9)
  Placement = pos=(0,30,9) rot=(1,0,0;1.5708rad)
  ReferenceAxis = -> Sketch011 [V_Axis]
  Reversed = true
  Sketch = -> Sketch011
FEATURE [Part::Cut] Cut009
  Base = -> Cut008
  Tool = -> Revolution005
FEATURE [Sketcher::SketchObject] Sketch012
  sketch-geometry (17):
    g0: Circle CenterX=0 CenterY=0 CenterZ=0 NormalX=0 NormalY=0 NormalZ=1 Radius=42.3378
    g1: Circle CenterX=24 CenterY=0 CenterZ=0 NormalX=0 NormalY=0 NormalZ=1 Radius=2.5
    g2: ArcOfCircle CenterX=0 CenterY=0 CenterZ=0 NormalX=0 NormalY=0 NormalZ=1 Radius=26.5 StartAngle=3.14118 EndAngle=4.71197
    g3: ArcOfCircle CenterX=0 CenterY=0 CenterZ=0 NormalX=0 NormalY=0 NormalZ=1 Radius=21.5 StartAngle=3.14118 EndAngle=4.71197
    g4: ArcOfCircle CenterX=-24 CenterY=0.00997847 CenterZ=0 NormalX=0 NormalY=0 NormalZ=1 Radius=2.5 StartAngle=6.28277 EndAngle=9.42436
    g5: ArcOfCircle CenterX=-0.00997847 CenterY=-24 CenterZ=0 NormalX=0 NormalY=0 NormalZ=1 Radius=2.5 StartAngle=4.71197 EndAngle=7.85357
    g6: LineSegment [constr] StartX=-26.5 StartY=0.0110179 StartZ=0 EndX=-21.5 EndY=0.00893904 EndZ=0
    g7: LineSegment [constr] StartX=0 StartY=0 StartZ=0 EndX=-21.5 EndY=0.00893904 EndZ=0
    g8: LineSegment [constr] StartX=-0.0110179 StartY=-26.5 StartZ=0 EndX=-0.00893904 EndY=-21.5 EndZ=0
    g9: LineSegment [constr] StartX=-0.00893904 StartY=-21.5 StartZ=0 EndX=0 EndY=0 EndZ=0
    g10: Circle CenterX=0 CenterY=0 CenterZ=0 NormalX=0 NormalY=0 NormalZ=1 Radius=4.66412
    g11: Circle CenterX=-24 CenterY=0.00997847 CenterZ=0 NormalX=0 NormalY=0 NormalZ=1 Radius=17
    g12: Circle CenterX=-0.00997847 CenterY=-24 CenterZ=0 NormalX=0 NormalY=0 NormalZ=1 Radius=17
    g13: Circle CenterX=24 CenterY=0 CenterZ=0 NormalX=0 NormalY=0 NormalZ=1 Radius=17
    g14: Circle CenterX=46.2535 CenterY=44.443 CenterZ=0 NormalX=0 NormalY=0 NormalZ=1 Radius=13.8646
    g15: Circle CenterX=52.704 CenterY=11.7414 CenterZ=0 NormalX=0 NormalY=0 NormalZ=1 Radius=13.9593
    g16: Circle CenterX=30.907 CenterY=-29.6319 CenterZ=0 NormalX=0 NormalY=0 NormalZ=1 Radius=14.4605
  constraints (32):
    c: Coincident(g0,g-1)
    c: PointOnObject(g1,g-1)
    c: Coincident(g2,g-1)
    c: Coincident(g3,g-1)
    c: Coincident(g2,g4)
    c: Coincident(g3,g4)
    c: Coincident(g2,g5)
    c: Coincident(g3,g5)
    c: Coincident(g6,g2)
    c: Coincident(g6,g3)
    c: PointOnObject(g4,g6)
    c: Coincident(g7,g-1)
    c: Coincident(g7,g3)
    c: Coincident(g8,g9)
    c: Coincident(g9,g-1)
    c: Coincident(g8,g3)
    c: Coincident(g8,g2)
    c: PointOnObject(g5,g8)
    c: Parallel(g8,g9)
    c: Parallel(g7,g6)
    c: Radius(g4) = 2.5
    c: Distance(g-1,g4) = 24
    c: Angle(g7,g9) = 1.5708
    c: Coincident(g10,g-1)
    c: Coincident(g11,g4)
    c: Radius(g11) = 17
    c: Coincident(g12,g5)
    c: Coincident(g13,g1)
    c: Equal(g13,g12)
    c: Equal(g12,g11)
    c: DistanceX(g-1,g1) = 24
    c: Radius(g1) = 2.5
FEATURE [Sketcher::SketchObject] Sketch013
  sketch-geometry (1):
    g0: Circle CenterX=0 CenterY=30.2023 CenterZ=0 NormalX=0 NormalY=0 NormalZ=1 Radius=14
  constraints (2):
    c: PointOnObject(g0,g-2)
    c: Radius(g0) = 14
